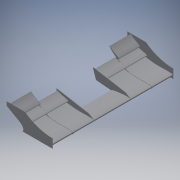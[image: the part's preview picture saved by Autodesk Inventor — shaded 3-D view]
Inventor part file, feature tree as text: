
AUTODESK INVENTOR PART (.ipt)
format: ipt  version: 2018.2 (Build 222227000, 227)  size: 749,056 bytes
history: native  units: mm
features: projected_geometry x11, extrude x8, sketch x8, mirror x1, other x1
ambient origin geometry x8: Origin, YZ Plane, XZ Plane, XY Plane, X Axis, Y Axis, Z Axis, Center Point
bodies: Body1 (feature_tree)
feature tree (29):
  extrude  "押し出し7"  Depth=394.0mm TaperAngle=0.0deg
  extrude  "押し出し8"  Depth=5.0mm TaperAngle=0.0deg
  extrude  "押し出し9"  Depth=225.0mm TaperAngle=0.0deg
  extrude  "押し出し10"  Depth=5.0mm TaperAngle=0.0deg
  extrude  "押し出し11"  Depth=225.0mm TaperAngle=0.0deg
  extrude  "押し出し12"  Depth=2.0mm TaperAngle=0.0deg
  extrude  "押し出し13"  Depth=2.0mm
  extrude  "押し出し14"  Depth=5.0mm
  mirror  "ミラー2"
  other  "ソリッド36"
  sketch  "スケッチ8"
  projected_geometry  "投影ループ7"
  sketch  "スケッチ9"
  projected_geometry  "投影ループ8"
  sketch  "スケッチ10"
  projected_geometry  "投影ループ9"
  projected_geometry  "投影ループ10"
  sketch  "スケッチ11"
  projected_geometry  "投影ループ11"
  sketch  "スケッチ12"
  projected_geometry  "投影ループ12"
  projected_geometry  "投影ループ13"
  projected_geometry  "投影ループ14"
  sketch  "スケッチ13"
  projected_geometry  "投影ループ15"
  sketch  "スケッチ14"
  projected_geometry  "投影ループ16"
  sketch  "スケッチ15"
  projected_geometry  "投影ループ17"
